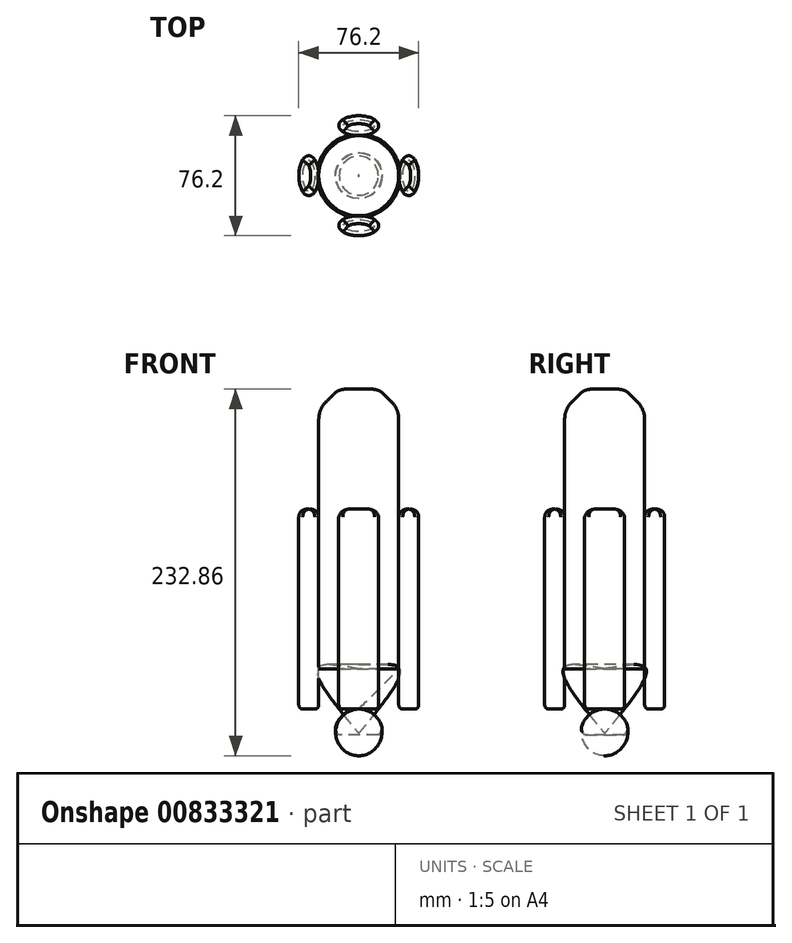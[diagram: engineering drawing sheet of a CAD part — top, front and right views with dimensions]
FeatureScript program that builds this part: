
annotation { "Feature Type Name" : "Feature", "Feature Type Description" : "" }
export const myFeature = defineFeature(function(context is Context, id is Id, definition is map)
    precondition{}
    {
        {
            var Q0;
            Q0=qCreatedBy(makeId("Top.planeOp"),FACE);
            var sketch = newSketch(context, id + "F0", { "sketchPlane" : qUnion([Q0])});
            skCircle(sketch, "E0", {"center": v(0, 0) * mm, "radius": 25.4 * mm});
            skEllipse(sketch, "E1", {"center": v(0.1, 31.75) * mm, "majorRadius": 12.7 * mm, "minorRadius": 6.35 * mm, "majorAxis": v(-1, 0)});
            skEllipse(sketch, "E2.MirrorC", {"center": v(0.1, -31.75) * mm, "majorRadius": 12.7 * mm, "minorRadius": 6.35 * mm, "majorAxis": v(-1, 0)});
            skSolve(sketch);
        }
        {
            var Q0;
            Q0=makeQuery(id+"F0.imprint","IMPRINT",FACE,{"disambiguationData":[TD([[makeQuery(id+"F0.imprint","IMPRINT",EDGE,{"derivedFrom":sQuery(id+"F0.wireOp",EDGE,"E0")}),1.0]])]});
            extrude(context, id + "F1", {"entities" : qUnion([Q0]), "depth" : 203.2 * mm, "offsetDistance" : 25.4 * mm});
        }
        {
            var Q0;
            Q0=qCreatedBy(makeId("Top.planeOp"),FACE);
            var sketch = newSketch(context, id + "F2", { "sketchPlane" : qUnion([Q0])});
            skEllipse(sketch, "E3", {"center": v(0, -31.75) * mm, "majorRadius": 12.7 * mm, "minorRadius": 6.35 * mm, "majorAxis": v(1, 0)});
            skEllipse(sketch, "E4", {"center": v(0, 31.75) * mm, "majorRadius": 12.7 * mm, "minorRadius": 6.35 * mm, "majorAxis": v(1, 0)});
            skSolve(sketch);
        }
        {
            var Q0;
            Q0=makeQuery(id+"F2.imprint","IMPRINT",FACE,{"disambiguationData":[TD([[makeQuery(id+"F2.imprint","IMPRINT",EDGE,{"derivedFrom":sQuery(id+"F2.wireOp",EDGE,"E3")}),1.0]])]});
            var Q1;
            Q1=makeQuery(id+"F2.imprint","IMPRINT",FACE,{"disambiguationData":[TD([[makeQuery(id+"F2.imprint","IMPRINT",EDGE,{"derivedFrom":sQuery(id+"F2.wireOp",EDGE,"E4")}),1.0]])]});
            extrude(context, id + "F3", {"entities" : qUnion([Q0, Q1]), "operationType" : NewBodyOperationType.ADD, "depth" : 127 * mm, "offsetDistance" : 25.4 * mm});
        }
        {
            var Q0;
            Q0=makeQuery(id+"F3.opExtrude","CAP_EDGE",EDGE,{"disambiguationData":[OSD([sQuery(id+"F2.wireOp",EDGE,"E3")])],"isStart":false});
            fillet(context, id + "F4", {"entities" : qUnion([Q0]), "radius" : 5.08 * mm, "tangentPropagation" : true, "allowEdgeOverflow" : false});
        }
        {
            var Q0;
            Q0=makeQuery(id+"F3.opExtrude","CAP_FACE",FACE,{"disambiguationData":[OSD([sQuery(id+"F2.wireOp",EDGE,"E4")])],"isStart":false});
            fillet(context, id + "F5", {"entities" : qUnion([Q0]), "radius" : 5.08 * mm, "tangentPropagation" : true, "allowEdgeOverflow" : false});
        }
        {
            var Q0;
            Q0=makeQuery(id+"F1.opExtrude","CAP_FACE",FACE,{"disambiguationData":[OSD([sQuery(id+"F0.wireOp",EDGE,"E0")])],"isStart":false});
            chamfer(context, id + "F6", {"entities" : qUnion([Q0]), "width" : 12.7 * mm, "tangentPropagation" : true});
        }
        {
            var Q0;
            {var subQ0=sQuery(id+"F0.wireOp",EDGE,"E0");Q0=makeQuery(id+"F6.opChamfer","BLEND_EDGE",EDGE,{"blendedFrom":[makeQuery(id+"F1.opExtrude","CAP_EDGE",EDGE,{"disambiguationData":[OSD([subQ0])],"isStart":false}),makeQuery(id+"F1.opExtrude","SWEPT_FACE",FACE,{"disambiguationData":[OSD([subQ0])]})],"blendedInto":[makeQuery(id+"F1.opExtrude","SWEPT_FACE",FACE,{"disambiguationData":[OSD([subQ0])]})]});}
            fillet(context, id + "F7", {"entities" : qUnion([Q0]), "radius" : 15.24 * mm, "tangentPropagation" : true, "allowEdgeOverflow" : false});
        }
        {
            var Q0;
            Q0=makeQuery(id+"F1.opExtrude","CAP_EDGE",EDGE,{"disambiguationData":[OSD([sQuery(id+"F0.wireOp",EDGE,"E0")])],"isStart":true});
            chamfer(context, id + "F8", {"entities" : qUnion([Q0]), "width" : 25.4 * mm, "tangentPropagation" : true});
        }
        {
            var Q0;
            Q0=qCreatedBy(makeId("Top.planeOp"),FACE);
            var sketch = newSketch(context, id + "F9", { "sketchPlane" : qUnion([Q0])});
            skEllipse(sketch, "E5", {"center": v(31.75, 0) * mm, "majorRadius": 12.7 * mm, "minorRadius": 6.35 * mm, "majorAxis": v(0, 1)});
            skSolve(sketch);
        }
        {
            var Q0;
            Q0=qCreatedBy(makeId("Top.planeOp"),FACE);
            var sketch = newSketch(context, id + "F10", { "sketchPlane" : qUnion([Q0])});
            skEllipse(sketch, "E6", {"center": v(-31.75, 0) * mm, "majorRadius": 12.7 * mm, "minorRadius": 6.35 * mm, "majorAxis": v(0, 1)});
            skSolve(sketch);
        }
        {
            var Q0;
            Q0=makeQuery(id+"F10.imprint","IMPRINT",FACE,{"disambiguationData":[TD([[makeQuery(id+"F10.imprint","IMPRINT",EDGE,{"derivedFrom":sQuery(id+"F10.wireOp",EDGE,"E6")}),1.0]])]});
            var Q1;
            Q1=makeQuery(id+"F9.imprint","IMPRINT",FACE,{"disambiguationData":[TD([[makeQuery(id+"F9.imprint","IMPRINT",EDGE,{"derivedFrom":sQuery(id+"F9.wireOp",EDGE,"E5")}),1.0]])]});
            extrude(context, id + "F11", {"entities" : qUnion([Q0, Q1]), "operationType" : NewBodyOperationType.ADD, "depth" : 127 * mm, "offsetDistance" : 25.4 * mm});
        }
        {
            var Q0;
            Q0=makeQuery(id+"F11.opExtrude","CAP_EDGE",EDGE,{"disambiguationData":[OSD([sQuery(id+"F9.wireOp",EDGE,"E5")])],"isStart":false});
            fillet(context, id + "F12", {"entities" : qUnion([Q0]), "radius" : 5.08 * mm, "tangentPropagation" : true, "allowEdgeOverflow" : false});
        }
        {
            var Q0;
            Q0=makeQuery(id+"F11.opExtrude","CAP_EDGE",EDGE,{"disambiguationData":[OSD([sQuery(id+"F10.wireOp",EDGE,"E6")])],"isStart":false});
            fillet(context, id + "F13", {"entities" : qUnion([Q0]), "radius" : 5.08 * mm, "tangentPropagation" : true, "allowEdgeOverflow" : false});
        }
        {
            var Q0;
            Q0=qCreatedBy(makeId("Right.planeOp"),FACE);
            var sketch = newSketch(context, id + "F14", { "sketchPlane" : qUnion([Q0])});
            skLineSegment(sketch, "E7", {"start": v(0, 0) * mm, "end": v(0, -29.66) * mm});
            skPoint(sketch, "E8.end.orphan", {"position": v(14.4, 0) * mm});
            skArc(sketch, "E9", {"start": v(0, -29.66) * mm, "mid": v(15, -14.83) * mm, "end": v(0, 0) * mm});
            skSolve(sketch);
        }
        {
            var Q0;
            Q0=makeQuery(id+"F14.imprint","IMPRINT",FACE,{"disambiguationData":[TD([[makeQuery(id+"F14.imprint","IMPRINT",EDGE,{"derivedFrom":sQuery(id+"F14.wireOp",EDGE,"E7")}),1.0]])]});
            var Q1;
            Q1=sQuery(id+"F14.wireOp",EDGE,"E7");
            revolve(context, id + "F15", {"surfaceOperationType" : NewSurfaceOperationType.NEW, "entities" : qUnion([Q0]), "axis" : qUnion([Q1]), "revolveType" : RevolveType.FULL});
        }
        {
            var Q0;
            Q0=qCreatedBy(makeId("Right.planeOp"),FACE);
            var sketch = newSketch(context, id + "F16", { "sketchPlane" : qUnion([Q0])});
            skLineSegment(sketch, "E10", {"start": v(0, 25.84) * mm, "end": v(0, -34.26) * mm});
            skFitSpline(sketch, "E11", {"points": [v(0, 25.84) * mm, v(26.06, 25.84) * mm, v(0, -15.4) * mm], "startDerivative": vector(84.28, 15.07) * mm, "endDerivative": vector(-75.97, -92.02) * mm});
            skSolve(sketch);
        }
        {
            var Q0;
            {var subQ0=sQuery(id+"F16.wireOp",EDGE,"E11");Q0=makeQuery(id+"F16.imprint","IMPRINT",FACE,{"disambiguationData":[TD([[makeQuery(id+"F16.imprint","IMPRINT",EDGE,{"derivedFrom":subQ0}),-1.0]])]});}
            var Q1;
            Q1=sQuery(id+"F16.wireOp",EDGE,"E10");
            revolve(context, id + "F17", {"surfaceOperationType" : NewSurfaceOperationType.NEW, "entities" : qUnion([Q0]), "axis" : qUnion([Q1]), "revolveType" : RevolveType.FULL});
        }
        {
            var Q0;
            Q0=qCreatedBy(makeId("Right.planeOp"),FACE);
            var sketch = newSketch(context, id + "F18", { "sketchPlane" : qUnion([Q0])});
            skLineSegment(sketch, "E12.bottom", {"start": v(-20.43, -16.37) * mm, "end": v(29.46, -16.37) * mm});
            skLineSegment(sketch, "E12.top", {"start": v(-20.43, -43.28) * mm, "end": v(29.46, -43.28) * mm});
            skLineSegment(sketch, "E12.left", {"start": v(-20.43, -16.37) * mm, "end": v(-20.43, -43.28) * mm});
            skLineSegment(sketch, "E12.right", {"start": v(29.46, -16.37) * mm, "end": v(29.46, -43.28) * mm});
            skSolve(sketch);
        }
        {
            var Q0;
            Q0=makeQuery(id+"F18.imprint","IMPRINT",FACE,{"disambiguationData":[TD([[makeQuery(id+"F18.imprint","IMPRINT",EDGE,{"derivedFrom":sQuery(id+"F18.wireOp",EDGE,"E12.bottom")}),-1.0]])]});
            extrude(context, id + "F19", {"entities" : qUnion([Q0]), "operationType" : NewBodyOperationType.REMOVE, "endBound" : BoundingType.SYMMETRIC, "depth" : 254 * mm, "offsetDistance" : 25.4 * mm});
        }
        {
            var Q0;
            {var subQ0=sQuery(id+"F0.wireOp",EDGE,"E0");Q0=makeQuery(id+"F6.opChamfer","BLEND_EDGE",EDGE,{"blendedFrom":[makeQuery(id+"F1.opExtrude","CAP_EDGE",EDGE,{"disambiguationData":[OSD([subQ0])],"isStart":false}),makeQuery(id+"F1.opExtrude","CAP_FACE",FACE,{"disambiguationData":[OSD([subQ0])],"isStart":false})],"blendedInto":[makeQuery(id+"F1.opExtrude","CAP_FACE",FACE,{"disambiguationData":[OSD([subQ0])],"isStart":false})]});}
            fillet(context, id + "F20", {"entities" : qUnion([Q0]), "radius" : 10.16 * mm, "tangentPropagation" : true, "allowEdgeOverflow" : false});
        }
        {
            var Q0;
            Q0=makeQuery(id+"F11.opExtrude","CAP_EDGE",EDGE,{"disambiguationData":[OSD([sQuery(id+"F10.wireOp",EDGE,"E6")])],"isStart":true});
            fillet(context, id + "F21", {"entities" : qUnion([Q0]), "radius" : 2.54 * mm, "tangentPropagation" : true, "allowEdgeOverflow" : false});
        }
        {
            var Q0;
            Q0=makeQuery(id+"F3.opExtrude","CAP_EDGE",EDGE,{"disambiguationData":[OSD([sQuery(id+"F2.wireOp",EDGE,"E3")])],"isStart":true});
            fillet(context, id + "F22", {"entities" : qUnion([Q0]), "radius" : 2.54 * mm, "tangentPropagation" : true, "allowEdgeOverflow" : false});
        }
        {
            var Q0;
            Q0=makeQuery(id+"F3.opExtrude","CAP_EDGE",EDGE,{"disambiguationData":[OSD([sQuery(id+"F2.wireOp",EDGE,"E4")])],"isStart":true});
            fillet(context, id + "F23", {"entities" : qUnion([Q0]), "radius" : 2.54 * mm, "tangentPropagation" : true, "allowEdgeOverflow" : false});
        }
        {
            var Q0;
            Q0=makeQuery(id+"F11.opExtrude","CAP_EDGE",EDGE,{"disambiguationData":[OSD([sQuery(id+"F9.wireOp",EDGE,"E5")])],"isStart":true});
            fillet(context, id + "F24", {"entities" : qUnion([Q0]), "radius" : 2.54 * mm, "tangentPropagation" : true, "allowEdgeOverflow" : false});
        }
        {
            var Q0;
            Q0=makeQuery(id+"F19.boolean.opBoolean","INTERSECT",EDGE,{"derivedFrom":[makeQuery(id+"F15.opRevolve","SWEPT_FACE",FACE,{"disambiguationData":[OSD([sQuery(id+"F14.wireOp",EDGE,"E9")])]}),makeQuery(id+"F19.opExtrude","SWEPT_FACE",FACE,{"disambiguationData":[OSD([sQuery(id+"F18.wireOp",EDGE,"E12.bottom")])]})]});
            chamfer(context, id + "F25", {"entities" : qUnion([Q0]), "width" : 2.54 * mm, "tangentPropagation" : true});
        }
        {
            var Q0;
            {var subQ0=makeQuery(id+"F15.opRevolve","SWEPT_FACE",FACE,{"disambiguationData":[OSD([sQuery(id+"F14.wireOp",EDGE,"E9")])]});Q0=makeQuery(id+"F25.opChamfer","BLEND_EDGE",EDGE,{"blendedFrom":[makeQuery(id+"F19.boolean.opBoolean","INTERSECT",EDGE,{"derivedFrom":[subQ0,makeQuery(id+"F19.opExtrude","SWEPT_FACE",FACE,{"disambiguationData":[OSD([sQuery(id+"F18.wireOp",EDGE,"E12.bottom")])]})]}),subQ0],"blendedInto":[subQ0]});}
            fillet(context, id + "F26", {"entities" : qUnion([Q0]), "radius" : 2.54 * mm, "tangentPropagation" : true, "allowEdgeOverflow" : false});
        }
    });
